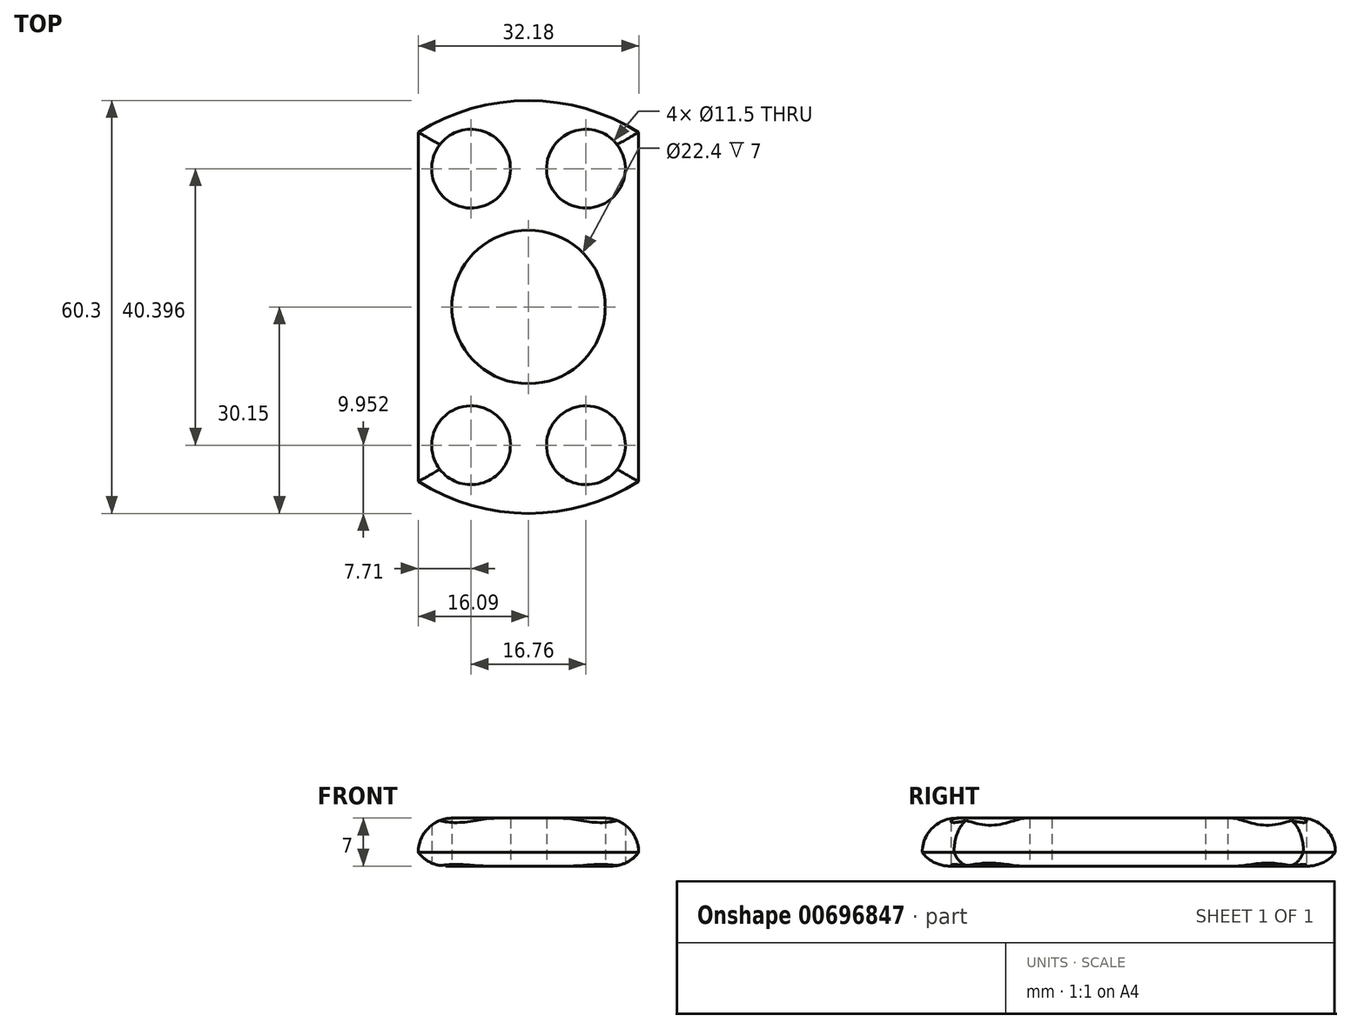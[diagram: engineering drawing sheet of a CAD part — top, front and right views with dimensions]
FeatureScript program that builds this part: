
annotation { "Feature Type Name" : "Feature", "Feature Type Description" : "" }
export const myFeature = defineFeature(function(context is Context, id is Id, definition is map)
    precondition{}
    {
        {
            var Q0;
            Q0=qCreatedBy(makeId("Top.planeOp"),FACE);
            var sketch = newSketch(context, id + "F0", { "sketchPlane" : qUnion([Q0])});
            skCircle(sketch, "E0", {"center": v(0, 0) * mm, "radius": 11.2 * mm});
            skArc(sketch, "E1", {"start": v(16.09, 25.5) * mm, "mid": v(0, 30.15) * mm, "end": v(-16.09, 25.5) * mm});
            skLineSegment(sketch, "E2", {"start": v(16.09, 25.5) * mm, "end": v(16.09, -25.5) * mm});
            skLineSegment(sketch, "E3.1.0", {"start": v(-16.09, -25.5) * mm, "end": v(-16.09, 25.5) * mm});
            skArc(sketch, "E4.trimOffspring", {"start": v(-16.09, -25.5) * mm, "mid": v(0, -30.15) * mm, "end": v(16.09, -25.5) * mm});
            skCircle(sketch, "E5", {"center": v(-8.38, 20.2) * mm, "radius": 5.75 * mm});
            skCircle(sketch, "E6.MirrorC", {"center": v(8.38, 20.2) * mm, "radius": 5.75 * mm});
            skCircle(sketch, "E7.MirrorC", {"center": v(-8.38, -20.2) * mm, "radius": 5.75 * mm});
            skCircle(sketch, "E8.MirrorC", {"center": v(8.38, -20.2) * mm, "radius": 5.75 * mm});
            skSolve(sketch);
        }
        {
            var Q0;
            Q0 = qSketchRegion(id + "F0", true);
            extrude(context, id + "F1", {"entities" : qUnion([Q0]), "depth" : 7 * mm, "offsetDistance" : 25 * mm});
        }
        {
            var Q0;
            Q0=makeQuery(id+"F1.opExtrude","CAP_EDGE",EDGE,{"disambiguationData":[OSD([sQuery(id+"F0.wireOp",EDGE,"E1")])],"isStart":false});
            var Q1;
            Q1=makeQuery(id+"F1.opExtrude","CAP_EDGE",EDGE,{"disambiguationData":[OSD([sQuery(id+"F0.wireOp",EDGE,"E3.1.0")])],"isStart":false});
            var Q2;
            Q2=makeQuery(id+"F1.opExtrude","CAP_EDGE",EDGE,{"disambiguationData":[OSD([sQuery(id+"F0.wireOp",EDGE,"E4.trimOffspring")])],"isStart":false});
            var Q3;
            Q3=makeQuery(id+"F1.opExtrude","CAP_EDGE",EDGE,{"disambiguationData":[OSD([sQuery(id+"F0.wireOp",EDGE,"E2")])],"isStart":false});
            fillet(context, id + "F2", {"entities" : qUnion([Q0, Q1, Q2, Q3]), "radius" : 5 * mm, "tangentPropagation" : true, "allowEdgeOverflow" : false});
        }
        {
            var Q0;
            Q0=makeQuery(id+"F1.opExtrude","CAP_EDGE",EDGE,{"disambiguationData":[OSD([sQuery(id+"F0.wireOp",EDGE,"E3.1.0")])],"isStart":true});
            var Q1;
            Q1=makeQuery(id+"F1.opExtrude","CAP_EDGE",EDGE,{"disambiguationData":[OSD([sQuery(id+"F0.wireOp",EDGE,"E1")])],"isStart":true});
            var Q2;
            Q2=makeQuery(id+"F1.opExtrude","CAP_EDGE",EDGE,{"disambiguationData":[OSD([sQuery(id+"F0.wireOp",EDGE,"E2")])],"isStart":true});
            var Q3;
            Q3=makeQuery(id+"F1.opExtrude","CAP_EDGE",EDGE,{"disambiguationData":[OSD([sQuery(id+"F0.wireOp",EDGE,"E4.trimOffspring")])],"isStart":true});
            fillet(context, id + "F3", {"entities" : qUnion([Q0, Q1, Q2, Q3]), "radius" : 5 * mm, "tangentPropagation" : true, "allowEdgeOverflow" : false});
        }
    });
